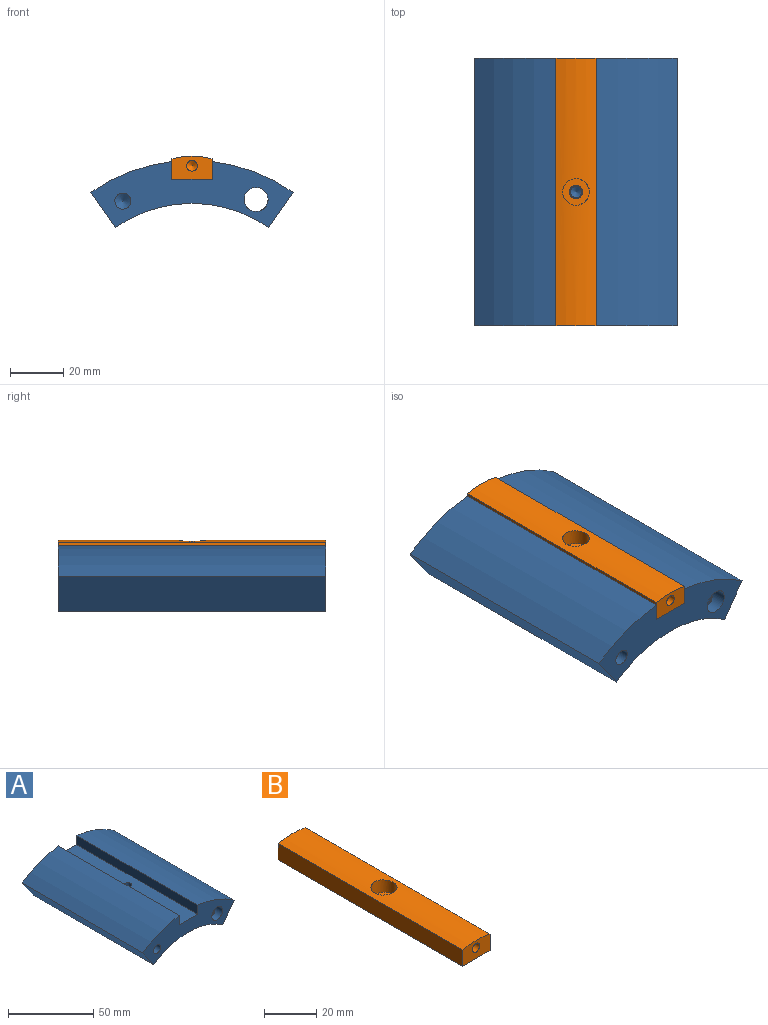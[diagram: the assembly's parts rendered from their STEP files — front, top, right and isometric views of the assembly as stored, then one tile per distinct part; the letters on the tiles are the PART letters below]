
ASSEMBLY  parts=2 mates=1
PART A: 34 faces, bbox 75.7x100x24.7 mm
  f0: plane 7.93x6.46mm, normal (0,-1,0), area 19.4mm2, adj f1,f7,f8,f22
  f1: cylinder r=1mm len=5.76mm, axis (-0.42,0,-0.91), area 7.9mm2, adj f0,f2,f8,f19,f22
  f2: plane 88x5.33mm, normal (0.91,0,-0.42), area 517.8mm2, adj f1,f3,f19,f22
  f3: cylinder r=1mm len=5.76mm, axis (-0.42,0,-0.91), area 7.9mm2, adj f2,f4,f8,f19,f22
  f4: plane 7.93x6.46mm, normal (0,1,0), area 19.4mm2, adj f3,f5,f8,f22
  f5: cylinder r=1mm len=6.46mm, axis (-0.42,0,-0.91), area 8.5mm2, adj f4,f6,f8,f18,f22
  f6: plane 88x6.04mm, normal (-0.91,0,0.42), area 586.7mm2, adj f5,f7,f18,f22
  f7: cylinder r=1mm len=6.46mm, axis (-0.42,0,-0.91), area 8.5mm2, adj f0,f6,f8,f18,f22
  f8: cylinder r=49.92mm len=100mm, axis (0,1,0), area 5315.7mm2, adj f0,f1,f3,f4,f5,f7,f11,f12
  f9: plane 100x6.57mm, normal (1,0,0), area 657.2mm2, adj f10,f15,f16,f17
  f10: cylinder r=66mm len=100mm, axis (0,1,0), area 3280.1mm2, adj f9,f11,f16,f17
  f11: plane 100x13.17mm, normal (-0.82,0,-0.57), area 1607.7mm2, adj f8,f10,f16,f17
  f12: plane 100x13.17mm, normal (0.82,0,-0.57), area 1607.7mm2, adj f8,f13,f16,f17
  f13: cylinder r=66mm len=100mm, axis (0,1,0), area 3280.1mm2, adj f12,f14,f16,f17
  f14: plane 100x6.57mm, normal (-1,0,0), area 657.2mm2, adj f13,f15,f16,f17
  f15: plane 100x15mm, normal (0,0,1), area 1486.1mm2, adj f9,f14,f16,f17,f21
  f16: plane 75.71x24.68mm, normal (0,-1,0), area 943.7mm2, adj f8,f9,f10,f11,f12,f13,f14,f15
  f17: plane 75.71x24.68mm, normal (0,1,0), area 972mm2, adj f8,f9,f10,f11,f12,f13,f14,f15
  f18: plane 89.01x0.12mm, normal (0.42,0,0.91), area 12.1mm2, adj f5,f6,f7,f8
  f19: plane 88.26x0.01mm, normal (0.42,0,0.91), area 0.7mm2, adj f1,f2,f3,f8
  f20: cone r=0mm half-angle=59deg, axis (0,0,1), area 16.2mm2, adj f21
  f21: cylinder r=2.1mm len=5mm, axis (0,0,1), area 66mm2, adj f15,f20
  f22: cylinder r=4.5mm len=100mm, axis (0,-1,0), area 551.9mm2, adj f0,f1,f2,f3,f4,f5,f6,f7
  f23: plane 90x8.02mm, normal (-0.42,0,-0.91), area 795.4mm2, adj f24,f25,f26,f27,f28,f29,f30,f31
  f24: cylinder r=1mm len=4.65mm, axis (-0.42,0,-0.91), area 5.4mm2, adj f22,f23,f25,f31
  f25: plane 88x4.23mm, normal (-0.91,0,0.42), area 410.7mm2, adj f22,f23,f24,f26
  f26: cylinder r=1mm len=4.65mm, axis (-0.42,0,-0.91), area 5.4mm2, adj f22,f23,f25,f27
  f27: plane 7.05x4.85mm, normal (0,1,0), area 6.7mm2, adj f22,f23,f26,f28
  f28: cylinder r=1mm len=3.94mm, axis (-0.42,0,-0.91), area 4.8mm2, adj f22,f23,f27,f29
  f29: plane 88x3.52mm, normal (0.91,0,-0.42), area 341.8mm2, adj f22,f23,f28,f30
  f30: cylinder r=1mm len=3.94mm, axis (-0.42,0,-0.91), area 4.8mm2, adj f22,f23,f29,f31
  f31: plane 7.05x4.85mm, normal (0,-1,0), area 6.7mm2, adj f22,f23,f24,f30
  f32: cone r=0mm half-angle=59deg, axis (0,-1,0), area 33mm2, adj f33
  f33: cylinder r=3mm len=55mm, axis (0,-1,0), area 1036.7mm2, adj f16,f32
PART B: 13 faces, bbox 15x100x8.5 mm
  f0: cylinder r=35mm len=100mm, axis (0,1,0), area 1433mm2, adj f2,f3,f4,f5,f6
  f1: plane 100x15mm, normal (0,0,-1), area 1480.4mm2, adj f2,f3,f4,f5,f8
  f2: plane 100x7.69mm, normal (1,0,0), area 768.7mm2, adj f0,f1,f4,f5
  f3: plane 100x7.69mm, normal (-1,0,0), area 768.7mm2, adj f0,f1,f4,f5
  f4: plane 15x8.5mm, normal (0,-1,0), area 110.9mm2, adj f0,f1,f2,f3,f9
  f5: plane 15x8.5mm, normal (0,1,0), area 110.9mm2, adj f0,f1,f2,f3,f11
  f6: cylinder r=5mm len=10mm, axis (0,0,1), area 182.9mm2, adj f0,f7
  f7: plane 10x10mm, normal (0,0,1), area 58.9mm2, adj f6,f8
  f8: cylinder r=2.5mm len=5mm, axis (0,0,1), area 39.3mm2, adj f1,f7
  f9: cylinder r=2mm len=10mm, axis (0,-1,0), area 125.7mm2, adj f4,f10
  f10: cone r=0mm half-angle=59deg, axis (0,-1,0), area 14.7mm2, adj f9
  f11: cylinder r=2mm len=10mm, axis (0,1,0), area 125.7mm2, adj f5,f12
  f12: cone r=0mm half-angle=59deg, axis (0,1,0), area 14.7mm2, adj f11
PLACE A t=(7.5,0,-59)mm
PLACE B at identity
MATE fastened B.f6 <-> A.f20  axis (0,0,-1) through (7.5,-50,0)mm
